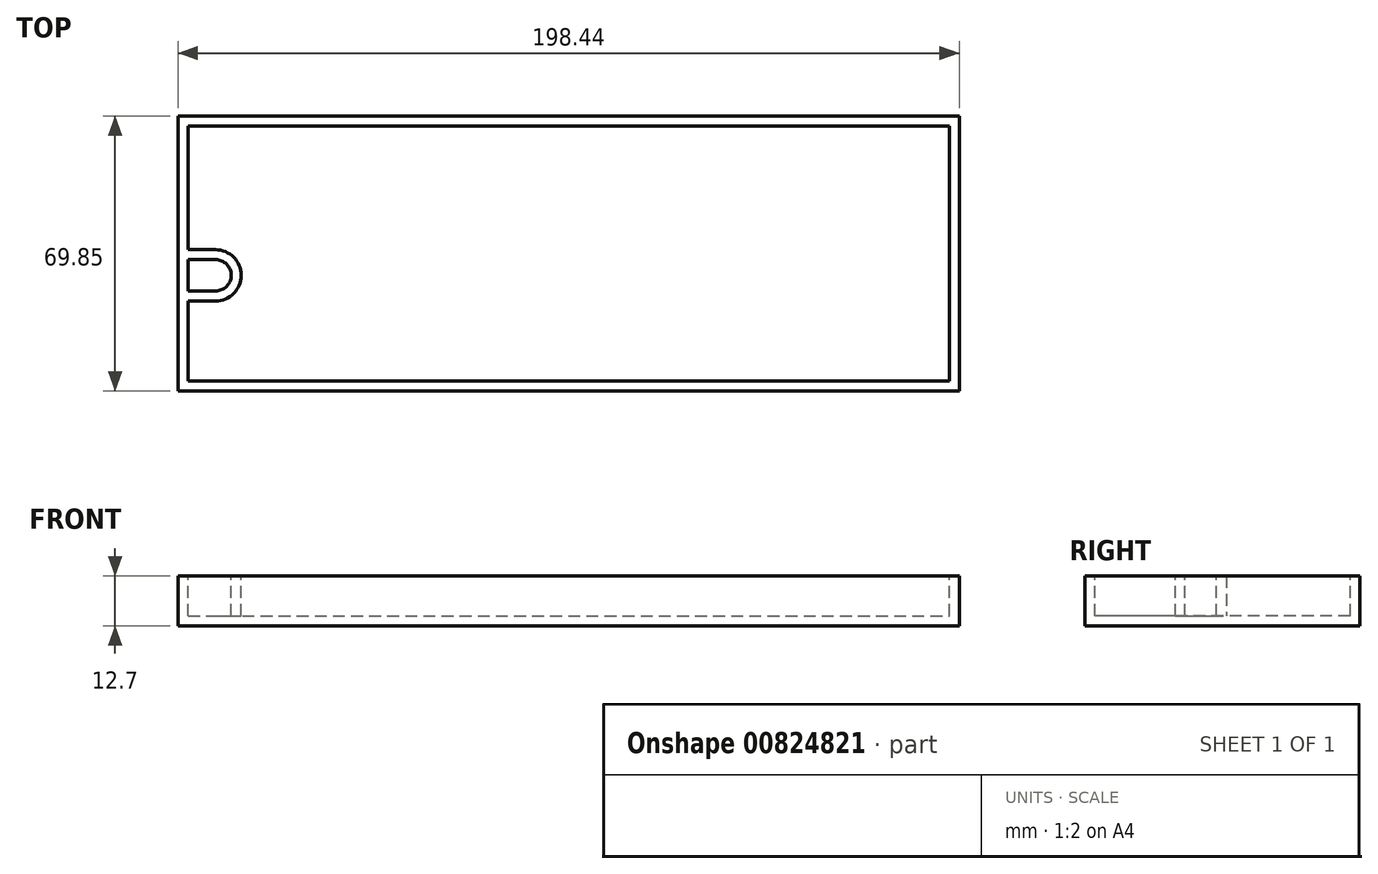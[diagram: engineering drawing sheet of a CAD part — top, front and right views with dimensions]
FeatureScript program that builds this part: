
annotation { "Feature Type Name" : "Feature", "Feature Type Description" : "" }
export const myFeature = defineFeature(function(context is Context, id is Id, definition is map)
    precondition{}
    {
        {
            var Q0;
            Q0=qCreatedBy(makeId("Top.planeOp"),FACE);
            var sketch = newSketch(context, id + "F0", { "sketchPlane" : qUnion([Q0])});
            skLineSegment(sketch, "E0.bottom", {"start": v(0, 0) * mm, "end": v(198.44, 0) * mm});
            skLineSegment(sketch, "E0.top", {"start": v(0, -69.85) * mm, "end": v(198.44, -69.85) * mm});
            skLineSegment(sketch, "E0.left", {"start": v(0, 0) * mm, "end": v(0, -69.85) * mm});
            skLineSegment(sketch, "E0.right", {"start": v(198.44, 0) * mm, "end": v(198.44, -69.85) * mm});
            skSolve(sketch);
        }
        {
            var Q0;
            Q0=qCreatedBy(makeId("Top.planeOp"),FACE);
            var sketch = newSketch(context, id + "F1", { "sketchPlane" : qUnion([Q0])});
            skLineSegment(sketch, "E1", {"start": v(0, 0) * mm, "end": v(0, -36.51) * mm});
            skLineSegment(sketch, "E2.bottom", {"start": v(0, -36.51) * mm, "end": v(9.53, -36.51) * mm});
            skLineSegment(sketch, "E2.top", {"start": v(0, -44.45) * mm, "end": v(9.53, -44.45) * mm});
            skLineSegment(sketch, "E2.left", {"start": v(0, -36.51) * mm, "end": v(0, -44.45) * mm});
            skLineSegment(sketch, "E2.right", {"start": v(9.53, -36.51) * mm, "end": v(9.53, -44.45) * mm});
            skCircle(sketch, "E3", {"center": v(9.53, -40.48) * mm, "radius": 3.97 * mm});
            skLineSegment(sketch, "E4", {"start": v(0, -36.51) * mm, "end": v(2.54, -36.51) * mm});
            skLineSegment(sketch, "E5", {"start": v(2.54, -44.45) * mm, "end": v(2.54, -36.51) * mm});
            skLineSegment(sketch, "E6", {"start": v(2.54, -36.51) * mm, "end": v(2.54, -33.97) * mm});
            skLineSegment(sketch, "E7", {"start": v(2.54, -33.97) * mm, "end": v(9.53, -33.97) * mm});
            skLineSegment(sketch, "E8", {"start": v(2.54, -44.45) * mm, "end": v(2.54, -47) * mm});
            skLineSegment(sketch, "E9", {"start": v(2.54, -47) * mm, "end": v(9.53, -47) * mm});
            skCircle(sketch, "E10", {"center": v(9.53, -40.48) * mm, "radius": 6.5 * mm});
            skLineSegment(sketch, "E11", {"start": v(198.25, 0) * mm, "end": v(198.25, -36.51) * mm});
            skSolve(sketch);
        }
        {
            var Q0;
            Q0=makeQuery(id+"F0.imprint","IMPRINT",FACE,{"disambiguationData":[TD([[makeQuery(id+"F0.imprint","IMPRINT",EDGE,{"derivedFrom":sQuery(id+"F0.wireOp",EDGE,"E0.bottom")}),-1.0]])]});
            extrude(context, id + "F2", {"entities" : qUnion([Q0]), "oppositeDirection" : true, "depth" : 12.7 * mm, "offsetDistance" : 25.4 * mm});
        }
        {
            var Q0;
            {var subQ0=sQuery(id+"F1.wireOp",EDGE,"E2.right");Q0=makeQuery(id+"F1.imprint","IMPRINT",FACE,{"disambiguationData":[TD([[makeQuery(id+"F1.imprint","IMPRINT",EDGE,{"derivedFrom":subQ0}),-1.0]])]});}
            var Q1;
            {var subQ2=sQuery(id+"F1.wireOp",EDGE,"E2.bottom");var subQ4=sQuery(id+"F1.wireOp",EDGE,"E10");var subQ5=makeQuery(id+"F1.imprint","INTERSECT",VERTEX,{"derivedFrom":[subQ2,subQ4]});Q1=makeQuery(id+"F1.imprint","IMPRINT",FACE,{"disambiguationData":[TD([[makeQuery(id+"F1.imprint","IMPRINT",EDGE,{"disambiguationData":[TD([[subQ5,-1.0]])],"derivedFrom":subQ4}),1.0]])]});}
            var Q2;
            {var subQ0=sQuery(id+"F1.wireOp",EDGE,"E5");Q2=makeQuery(id+"F1.imprint","IMPRINT",FACE,{"disambiguationData":[TD([[makeQuery(id+"F1.imprint","IMPRINT",EDGE,{"derivedFrom":subQ0}),-1.0]])]});}
            var Q3;
            {var subQ0=sQuery(id+"F1.wireOp",EDGE,"E2.right");Q3=makeQuery(id+"F1.imprint","IMPRINT",FACE,{"disambiguationData":[TD([[makeQuery(id+"F1.imprint","IMPRINT",EDGE,{"derivedFrom":subQ0}),1.0]])]});}
            extrude(context, id + "F3", {"entities" : qUnion([Q0, Q1, Q2, Q3]), "operationType" : NewBodyOperationType.REMOVE, "oppositeDirection" : true, "depth" : 10.16 * mm, "offsetDistance" : 25.4 * mm});
        }
        {
            var Q0;
            Q0=makeQuery(id+"F2.opExtrude","CAP_FACE",FACE,{"disambiguationData":[OSD([sQuery(id+"F0.wireOp",EDGE,"E0.bottom"),sQuery(id+"F0.wireOp",EDGE,"E0.top"),sQuery(id+"F0.wireOp",EDGE,"E0.left"),sQuery(id+"F0.wireOp",EDGE,"E0.right")])],"isStart":true});
            shell(context, id + "F4", {"entities" : qUnion([Q0]), "thickness" : 2.54 * mm});
        }
    });
